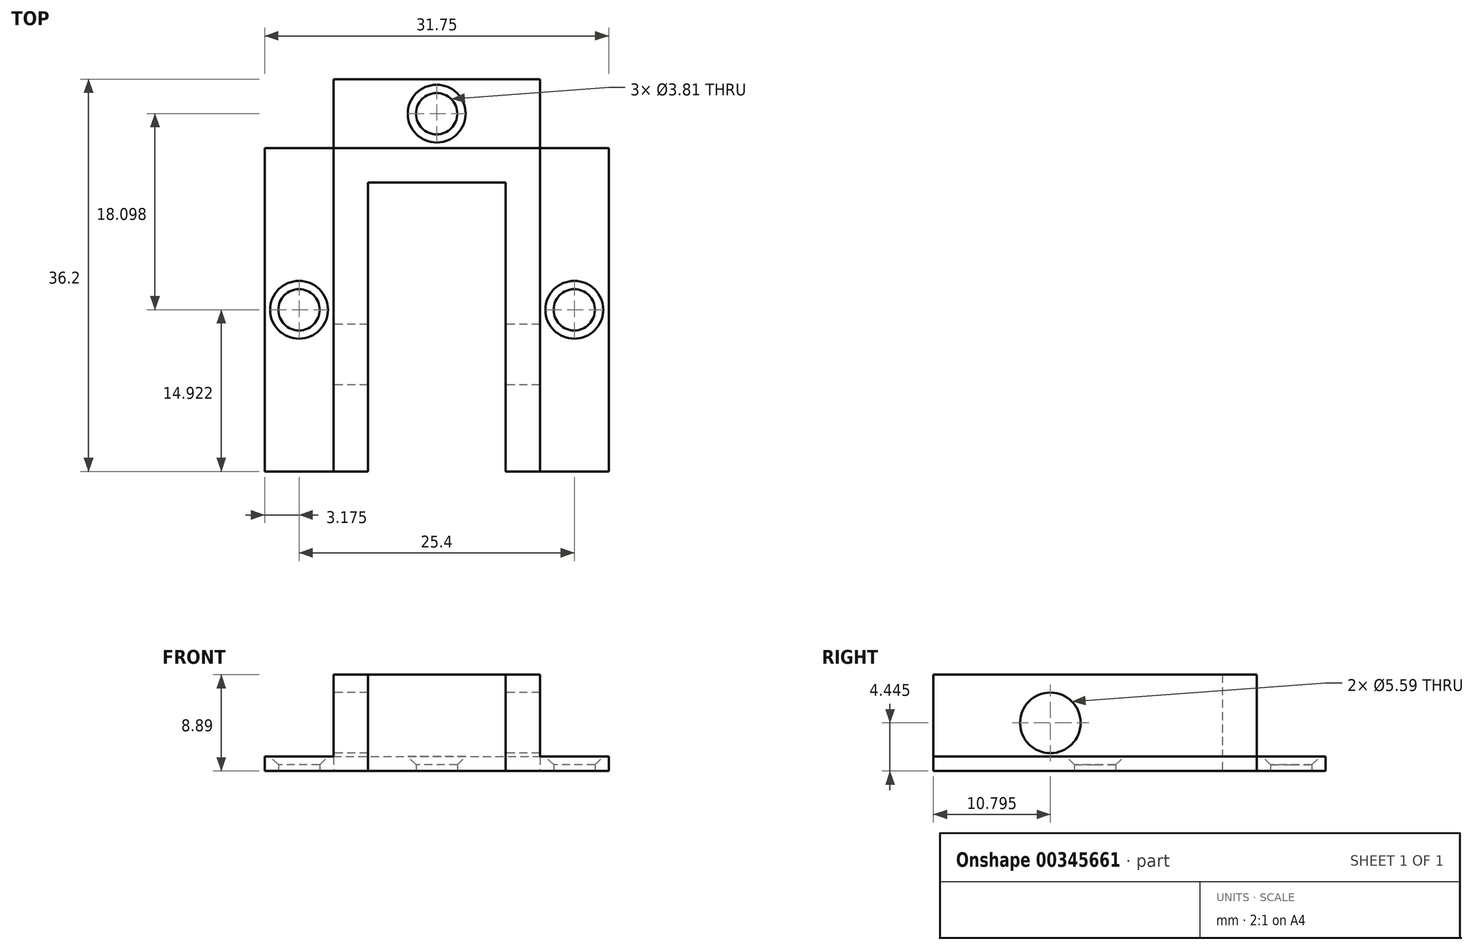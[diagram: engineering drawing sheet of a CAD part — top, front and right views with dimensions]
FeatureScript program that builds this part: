
annotation { "Feature Type Name" : "Feature", "Feature Type Description" : "" }
export const myFeature = defineFeature(function(context is Context, id is Id, definition is map)
    precondition{}
    {
        {
            var Q0;
            Q0=qCreatedBy(makeId("Top.planeOp"),FACE);
            var sketch = newSketch(context, id + "F0", { "sketchPlane" : qUnion([Q0])});
            skLineSegment(sketch, "E0", {"start": v(0, 0) * mm, "end": v(0, 29.85) * mm});
            skLineSegment(sketch, "E1", {"start": v(0, 29.85) * mm, "end": v(19.05, 29.85) * mm});
            skLineSegment(sketch, "E2", {"start": v(19.05, 29.85) * mm, "end": v(19.05, 0) * mm});
            skLineSegment(sketch, "E3", {"start": v(19.05, 0) * mm, "end": v(15.88, 0) * mm});
            skLineSegment(sketch, "E4", {"start": v(15.88, 0) * mm, "end": v(15.88, 26.67) * mm});
            skLineSegment(sketch, "E5", {"start": v(15.88, 26.67) * mm, "end": v(3.17, 26.67) * mm});
            skLineSegment(sketch, "E6", {"start": v(3.17, 26.67) * mm, "end": v(3.17, 0) * mm});
            skLineSegment(sketch, "E7", {"start": v(3.17, 0) * mm, "end": v(0, 0) * mm});
            skLineSegment(sketch, "E8", {"start": v(0, 0) * mm, "end": v(-6.35, 0) * mm});
            skLineSegment(sketch, "E9", {"start": v(-6.35, 0) * mm, "end": v(-6.35, 29.85) * mm});
            skLineSegment(sketch, "E10", {"start": v(-6.35, 29.85) * mm, "end": v(0, 29.85) * mm});
            skLineSegment(sketch, "E11", {"start": v(0, 29.85) * mm, "end": v(0, 36.2) * mm});
            skLineSegment(sketch, "E12", {"start": v(0, 36.2) * mm, "end": v(19.05, 36.2) * mm});
            skLineSegment(sketch, "E13", {"start": v(19.05, 36.2) * mm, "end": v(19.05, 29.85) * mm});
            skLineSegment(sketch, "E14", {"start": v(19.05, 29.85) * mm, "end": v(25.4, 29.85) * mm});
            skLineSegment(sketch, "E15", {"start": v(25.4, 29.85) * mm, "end": v(25.4, 0) * mm});
            skLineSegment(sketch, "E16", {"start": v(25.4, 0) * mm, "end": v(19.05, 0) * mm});
            skCircle(sketch, "E17", {"center": v(-3.18, 14.92) * mm, "radius": 1.9 * mm});
            skPoint(sketch, "E17.centerSnap0", {"position": v(-6.35, 14.92) * mm});
            skPoint(sketch, "E17.centerSnap1", {"position": v(-3.18, 0) * mm});
            skCircle(sketch, "E18", {"center": v(22.22, 14.92) * mm, "radius": 1.9 * mm});
            skPoint(sketch, "E18.centerSnap0", {"position": v(22.23, 0) * mm});
            skCircle(sketch, "E19", {"center": v(9.52, 33.02) * mm, "radius": 1.9 * mm});
            skPoint(sketch, "E19.centerSnap0", {"position": v(9.53, 29.85) * mm});
            skPoint(sketch, "E19.centerSnap1", {"position": v(0, 33.02) * mm});
            skSolve(sketch);
        }
        {
            var Q0;
            Q0=makeQuery(id+"F0.imprint","IMPRINT",FACE,{"disambiguationData":[TD([[makeQuery(id+"F0.imprint","IMPRINT",EDGE,{"derivedFrom":sQuery(id+"F0.wireOp",EDGE,"E0")}),-1.0]])]});
            extrude(context, id + "F1", {"entities" : qUnion([Q0]), "depth" : 8.9 * mm});
        }
        {
            var Q0;
            Q0=qCreatedBy(makeId("Right.planeOp"),FACE);
            var sketch = newSketch(context, id + "F2", { "sketchPlane" : qUnion([Q0])});
            skCircle(sketch, "E20", {"center": v(10.8, 4.45) * mm, "radius": 2.8 * mm});
            skSolve(sketch);
        }
        {
            var Q0;
            Q0=makeQuery(id+"F2.imprint","IMPRINT",FACE,{"disambiguationData":[TD([[makeQuery(id+"F2.imprint","IMPRINT",EDGE,{"derivedFrom":sQuery(id+"F2.wireOp",EDGE,"E20")}),1.0]])]});
            extrude(context, id + "F3", {"entities" : qUnion([Q0]), "operationType" : NewBodyOperationType.REMOVE, "depth" : 20.32 * mm});
        }
        {
            var Q0;
            Q0=makeQuery(id+"F0.imprint","IMPRINT",FACE,{"disambiguationData":[TD([[makeQuery(id+"F0.imprint","IMPRINT",EDGE,{"derivedFrom":sQuery(id+"F0.wireOp",EDGE,"E0")}),1.0]])]});
            var Q1;
            Q1=makeQuery(id+"F0.imprint","IMPRINT",FACE,{"disambiguationData":[TD([[makeQuery(id+"F0.imprint","IMPRINT",EDGE,{"derivedFrom":sQuery(id+"F0.wireOp",EDGE,"E1")}),1.0]])]});
            var Q2;
            Q2=makeQuery(id+"F0.imprint","IMPRINT",FACE,{"disambiguationData":[TD([[makeQuery(id+"F0.imprint","IMPRINT",EDGE,{"derivedFrom":sQuery(id+"F0.wireOp",EDGE,"E2")}),1.0]])]});
            extrude(context, id + "F4", {"entities" : qUnion([Q0, Q1, Q2]), "operationType" : NewBodyOperationType.ADD, "depth" : 1.33 * mm});
        }
        {
            var Q0;
            Q0=makeQuery(id+"F4.opExtrude","CAP_EDGE",EDGE,{"disambiguationData":[OSD([sQuery(id+"F0.wireOp",EDGE,"E18")])],"isStart":false});
            var Q1;
            Q1=makeQuery(id+"F4.opExtrude","CAP_EDGE",EDGE,{"disambiguationData":[OSD([sQuery(id+"F0.wireOp",EDGE,"E17")])],"isStart":false});
            var Q2;
            Q2=makeQuery(id+"F4.opExtrude","CAP_EDGE",EDGE,{"disambiguationData":[OSD([sQuery(id+"F0.wireOp",EDGE,"E19")])],"isStart":false});
            chamfer(context, id + "F5", {"entities" : qUnion([Q0, Q1, Q2]), "width" : 0.76 * mm, "tangentPropagation" : true});
        }
    });
